# Revit family: Pump Stations - ACLP Series
name_source: partatom
category: Equipamento especial
units: mm (PartAtom-declared; Revit-internal decimal feet)

## family parameters
Com base no plano de trabalho = Não
Compartilhado = Não
Corte com vazios quando carregada = Não
Cota do conector redondo = Utilizar diâmetro
Número OmniClass = 23.40.00.00
Ponto de cálculo do ambiente = Não
Sempre na vertical = Sim
Tipo de parte = Normal
Título OmniClass = Equipment and Furnishings

## types (1)
- ACLP Series
    Aluminium = Aluminium
    Box Heigth = 85
    Box Lenght = 153
    Box Visibility = Sim
    Box Width = 69
    Concrete = Concrete
    Corrente de Saída = 2 A
    DTT1 = 15
    DTT2 = 0
    DTT3 = 87
    DTT4 = 0
    DTT5 = 50
    DTT6 = 29
    DTT8 = 22
    Elevação padrão = 0
    Metal = Metal
    Modelo = ACLP
    RainBird: Description = Pump Stations - ACLP Series
    RainBird: Product Link = https://www.rainbird.com
    Slab Heigth = 10
    Slab Length = 165
    Slab Width = 129
    SupportProjetos: Level of Detail = LOD 300
    SupportProjetos: Review = R00
    Tipo de imagem = <Nenhum>
    URL = www.rainbird.com
    x = 2
    y = 64

## geometry (parser evidence)
native form markers: Blend x6, Sweep x24
no freeform markers — native parametric forms only
